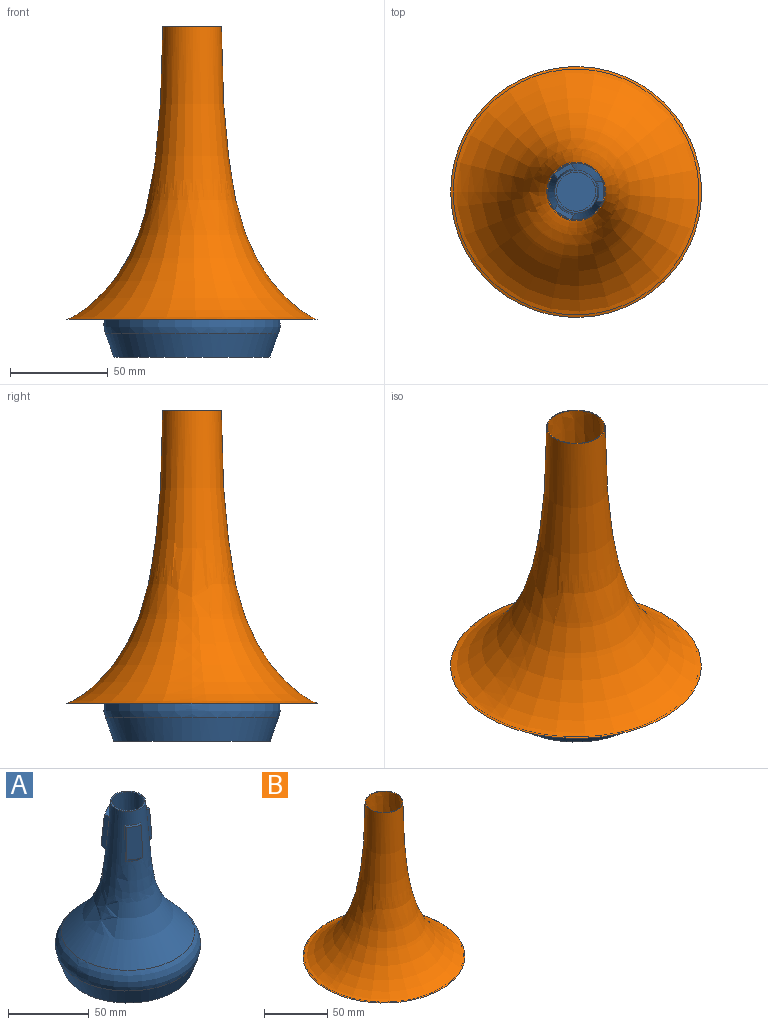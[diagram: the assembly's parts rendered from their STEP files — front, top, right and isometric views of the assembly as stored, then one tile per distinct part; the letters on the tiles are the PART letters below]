
ASSEMBLY  parts=2 mates=1
PART A: 30 faces, bbox 94.9x94.9x129.6 mm
  f0: plane 0.9x0.77mm, normal (-0.05,-0.08,-1), area 0.1mm2, adj f1,f2,f6
  f1: bspline ~10.85x7.71mm, area 39.9mm2, adj f0,f2,f4,f5,f6,f15
  f2: plane 30.82x9.28mm, normal (-0.87,0.5,0), area 83.9mm2, adj f0,f1,f3,f6,f15
  f3: plane 10.53x8.08mm, normal (0.05,0.08,1), area 25.8mm2, adj f2,f4,f6,f15
  f4: plane 30.82x9.28mm, normal (0.87,-0.5,0), area 83.9mm2, adj f1,f3,f5,f6,f15
  f5: plane 1.05x0.52mm, normal (-0.05,-0.08,-1), area 0.1mm2, adj f1,f4,f6
  f6: plane 23.38x9.7mm, normal (-0.5,-0.86,0.09), area 232.5mm2, adj f0,f1,f2,f3,f4,f5
  f7: plane 1.05x0.52mm, normal (-0.05,0.08,-1), area 0.1mm2, adj f8,f9,f13
  f8: bspline ~10.85x7.71mm, area 39.9mm2, adj f7,f9,f11,f12,f13,f15
  f9: plane 30.82x9.28mm, normal (0.87,0.5,0), area 83.9mm2, adj f7,f8,f10,f13,f15
  f10: plane 10.53x8.08mm, normal (0.05,-0.08,1), area 25.8mm2, adj f9,f11,f13,f15
  f11: plane 30.82x9.28mm, normal (-0.87,-0.5,0), area 83.9mm2, adj f8,f10,f12,f13,f15
  f12: plane 0.9x0.77mm, normal (-0.05,0.08,-1), area 0.1mm2, adj f8,f11,f13
  f13: plane 23.38x9.7mm, normal (-0.5,0.86,0.09), area 232.5mm2, adj f7,f8,f9,f10,f11,f12
  f14: plane 1.04x0.29mm, normal (0.09,0,-1), area 0.1mm2, adj f24,f28,f29
  f15: revolved ~99.34x82.48mm, area 25265.3mm2, adj f1,f2,f3,f4,f8,f9,f10,f11
  f16: plane 78.59x78.59mm, normal (0,0,1), area 4851mm2, adj f21
  f17: plane 80x80mm, normal (0,0,-1), area 5026.5mm2, adj f18
  f18: revolved ~88.64x88.64mm, area 3419.8mm2, adj f17,f23
  f19: plane 22x22mm, normal (0,0,1), area 66.1mm2, adj f15,f20
  f20: revolved ~99.62x80.2mm, area 12360.3mm2, adj f19,f22
  f21: revolved ~86.33x86.33mm, area 2995mm2, adj f16,f22
  f22: bspline ~88.03x87.98mm, area 3975.7mm2, adj f20,f21
  f23: bspline ~90.33x90.28mm, area 4085mm2, adj f15,f18
  f24: plane 30.82x10.01mm, normal (0,-1,0), area 83.9mm2, adj f14,f15,f25,f28,f29
  f25: plane 10.2x3.53mm, normal (-0.09,0,1), area 25.8mm2, adj f15,f24,f26,f28
  f26: plane 30.82x10.01mm, normal (0,1,0), area 83.9mm2, adj f15,f25,f27,f28,f29
  f27: plane 1.04x0.29mm, normal (0.09,0,-1), area 0.1mm2, adj f26,f28,f29
  f28: plane 23.38x10mm, normal (1,0,0.09), area 232.5mm2, adj f14,f24,f25,f26,f27,f29
  f29: bspline ~12.16x3.64mm, area 39.9mm2, adj f14,f15,f24,f26,f27,f28
PART B: 4 faces, bbox 128.5x128.5x150 mm
  f0: cone r=14.6mm half-angle=87.2deg, axis (0,0,1), area 37.2mm2, adj f1,f3
  f1: revolved ~149.98x125.94mm, area 27616.5mm2, adj f0,f2
  f2: plane 128.5x128.5mm, normal (0,0,-1), area 512.1mm2, adj f1,f3
  f3: revolved ~150x128.5mm, area 28357mm2, adj f0,f2
PLACE A t=(-26.39,-7.47,-37.01)mm
PLACE B t=(-26.39,-7.47,-17.57)mm
MATE slider B.f0 <-> A.f19  axis (0,0,-1) through (-26.39,-7.47,-18.05)mm
